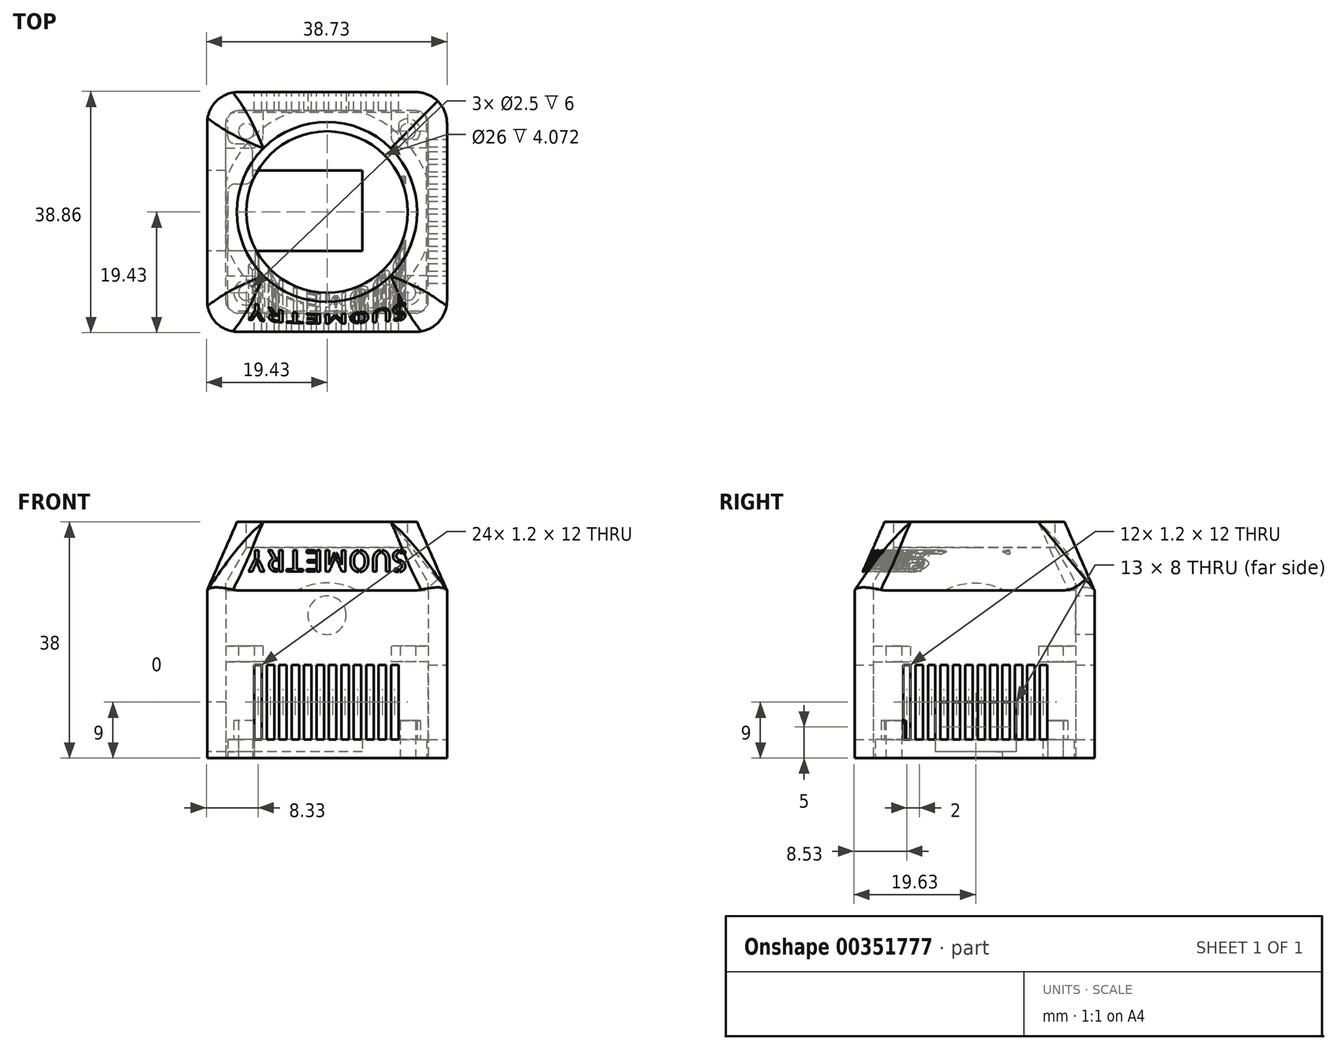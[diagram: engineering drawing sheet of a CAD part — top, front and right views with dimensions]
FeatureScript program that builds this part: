
annotation { "Feature Type Name" : "Feature", "Feature Type Description" : "" }
export const myFeature = defineFeature(function(context is Context, id is Id, definition is map)
    precondition{}
    {
        {
            var Q0;
            Q0=qCreatedBy(makeId("Top.planeOp"),FACE);
            var sketch = newSketch(context, id + "F0", { "sketchPlane" : qUnion([Q0])});
            skLineSegment(sketch, "E0.bottom", {"start": v(16, -16) * mm, "end": v(-16, -16) * mm});
            skLineSegment(sketch, "E0.top", {"start": v(16, 16) * mm, "end": v(-16, 16) * mm});
            skLineSegment(sketch, "E0.left", {"start": v(16, -16) * mm, "end": v(16, 16) * mm});
            skLineSegment(sketch, "E0.right", {"start": v(-16, -16) * mm, "end": v(-16, 16) * mm});
            skPoint(sketch, "E0.middle", {"position": v(0, 0) * mm});
            skCircle(sketch, "E1", {"center": v(-13, 13) * mm, "radius": 1.25 * mm});
            skCircle(sketch, "E2", {"center": v(13, 13) * mm, "radius": 1.25 * mm});
            skCircle(sketch, "E3", {"center": v(13, -13) * mm, "radius": 1.25 * mm});
            skCircle(sketch, "E4", {"center": v(-13, -13) * mm, "radius": 1.25 * mm});
            skLineSegment(sketch, "E5.bottom", {"start": v(-16, 4.5) * mm, "end": v(-12, 4.5) * mm});
            skLineSegment(sketch, "E5.top", {"start": v(-16, 11) * mm, "end": v(-12, 11) * mm});
            skLineSegment(sketch, "E5.left", {"start": v(-16, 4.5) * mm, "end": v(-16, 11) * mm});
            skLineSegment(sketch, "E5.right", {"start": v(-12, 4.5) * mm, "end": v(-12, 11) * mm});
            skSolve(sketch);
        }
        {
            var Q0;
            {var subQ4=sQuery(id+"F0.wireOp",EDGE,"E0.bottom");Q0=makeQuery(id+"F0.imprint","IMPRINT",FACE,{"disambiguationData":[TD([[makeQuery(id+"F0.imprint","IMPRINT",EDGE,{"derivedFrom":subQ4}),-1.0]])]});}
            var Q1;
            Q1=makeQuery(id+"F0.imprint","IMPRINT",FACE,{"disambiguationData":[TD([[makeQuery(id+"F0.imprint","IMPRINT",EDGE,{"derivedFrom":sQuery(id+"F0.wireOp",EDGE,"E4")}),1.0]])]});
            var Q2;
            Q2=makeQuery(id+"F0.imprint","IMPRINT",FACE,{"disambiguationData":[TD([[makeQuery(id+"F0.imprint","IMPRINT",EDGE,{"derivedFrom":sQuery(id+"F0.wireOp",EDGE,"E3")}),1.0]])]});
            var Q3;
            Q3=makeQuery(id+"F0.imprint","IMPRINT",FACE,{"disambiguationData":[TD([[makeQuery(id+"F0.imprint","IMPRINT",EDGE,{"derivedFrom":sQuery(id+"F0.wireOp",EDGE,"E2")}),1.0]])]});
            var Q4;
            Q4=makeQuery(id+"F0.imprint","IMPRINT",FACE,{"disambiguationData":[TD([[makeQuery(id+"F0.imprint","IMPRINT",EDGE,{"derivedFrom":sQuery(id+"F0.wireOp",EDGE,"E1")}),1.0]])]});
            extrude(context, id + "F1", {"entities" : qUnion([Q0, Q1, Q2, Q3, Q4]), "depth" : 3 * mm, "offsetDistance" : 25 * mm});
        }
        {
            var Q0;
            Q0=qCreatedBy(makeId("Top.planeOp"),FACE);
            var sketch = newSketch(context, id + "F2", { "sketchPlane" : qUnion([Q0])});
            skLineSegment(sketch, "E6.bottom", {"start": v(16.3, -16.3) * mm, "end": v(-16.3, -16.3) * mm});
            skLineSegment(sketch, "E6.top", {"start": v(16.3, 16.3) * mm, "end": v(-16.3, 16.3) * mm});
            skLineSegment(sketch, "E6.left", {"start": v(16.3, -16.3) * mm, "end": v(16.3, 16.3) * mm});
            skLineSegment(sketch, "E6.right", {"start": v(-16.3, -16.3) * mm, "end": v(-16.3, 16.3) * mm});
            skPoint(sketch, "E6.middle", {"position": v(0, 0) * mm});
            skLineSegment(sketch, "E7.0", {"start": v(19.3, 19.3) * mm, "end": v(-19.3, 19.3) * mm});
            skLineSegment(sketch, "E7.1", {"start": v(19.3, -19.3) * mm, "end": v(19.3, 19.3) * mm});
            skLineSegment(sketch, "E7.2", {"start": v(19.3, -19.3) * mm, "end": v(-19.3, -19.3) * mm});
            skLineSegment(sketch, "E7.3", {"start": v(-19.3, -19.3) * mm, "end": v(-19.3, 19.3) * mm});
            skLineSegment(sketch, "E8.bottom", {"start": v(-16.3, -16.3) * mm, "end": v(-10.3, -16.3) * mm});
            skLineSegment(sketch, "E8.top", {"start": v(-16.3, -10.3) * mm, "end": v(-10.3, -10.3) * mm});
            skLineSegment(sketch, "E8.left", {"start": v(-16.3, -16.3) * mm, "end": v(-16.3, -10.3) * mm});
            skLineSegment(sketch, "E8.right", {"start": v(-10.3, -16.3) * mm, "end": v(-10.3, -10.3) * mm});
            skLineSegment(sketch, "E9.bottom", {"start": v(-16.3, 16.3) * mm, "end": v(-10.3, 16.3) * mm});
            skLineSegment(sketch, "E9.top", {"start": v(-16.3, 10.3) * mm, "end": v(-10.3, 10.3) * mm});
            skLineSegment(sketch, "E9.left", {"start": v(-16.3, 16.3) * mm, "end": v(-16.3, 10.3) * mm});
            skLineSegment(sketch, "E9.right", {"start": v(-10.3, 16.3) * mm, "end": v(-10.3, 10.3) * mm});
            skLineSegment(sketch, "E10.bottom", {"start": v(16.3, 16.3) * mm, "end": v(10.3, 16.3) * mm});
            skLineSegment(sketch, "E10.top", {"start": v(16.3, 10.3) * mm, "end": v(10.3, 10.3) * mm});
            skLineSegment(sketch, "E10.left", {"start": v(16.3, 16.3) * mm, "end": v(16.3, 10.3) * mm});
            skLineSegment(sketch, "E10.right", {"start": v(10.3, 16.3) * mm, "end": v(10.3, 10.3) * mm});
            skLineSegment(sketch, "E11.bottom", {"start": v(16.3, -16.3) * mm, "end": v(10.3, -16.3) * mm});
            skLineSegment(sketch, "E11.top", {"start": v(16.3, -10.3) * mm, "end": v(10.3, -10.3) * mm});
            skLineSegment(sketch, "E11.left", {"start": v(16.3, -16.3) * mm, "end": v(16.3, -10.3) * mm});
            skLineSegment(sketch, "E11.right", {"start": v(10.3, -16.3) * mm, "end": v(10.3, -10.3) * mm});
            skSolve(sketch);
        }
        {
            var Q0;
            Q0=makeQuery(id+"F2.imprint","IMPRINT",FACE,{"disambiguationData":[TD([[makeQuery(id+"F2.imprint","IMPRINT",EDGE,{"derivedFrom":sQuery(id+"F2.wireOp",EDGE,"E6.bottom")}),1.0]])]});
            var sketch = newSketch(context, id + "F3", { "sketchPlane" : qUnion([Q0])});
            skCircle(sketch, "E12", {"center": v(13, -13) * mm, "radius": 2 * mm});
            skCircle(sketch, "E13", {"center": v(-13, -13) * mm, "radius": 2 * mm});
            skCircle(sketch, "E14", {"center": v(13, 13) * mm, "radius": 2 * mm});
            skCircle(sketch, "E15", {"center": v(-13, 13) * mm, "radius": 1.27 * mm});
            skSolve(sketch);
        }
        {
            var Q0;
            Q0=makeQuery(id+"F3.imprint","IMPRINT",FACE,{"disambiguationData":[TD([[makeQuery(id+"F3.imprint","IMPRINT",EDGE,{"derivedFrom":sQuery(id+"F3.wireOp",EDGE,"E13")}),1.0]])]});
            var Q1;
            Q1=makeQuery(id+"F3.imprint","IMPRINT",FACE,{"disambiguationData":[TD([[makeQuery(id+"F3.imprint","IMPRINT",EDGE,{"derivedFrom":sQuery(id+"F3.wireOp",EDGE,"E12")}),1.0]])]});
            var Q2;
            Q2=makeQuery(id+"F3.imprint","IMPRINT",FACE,{"disambiguationData":[TD([[makeQuery(id+"F3.imprint","IMPRINT",EDGE,{"derivedFrom":sQuery(id+"F3.wireOp",EDGE,"E14")}),1.0]])]});
            extrude(context, id + "F4", {"entities" : qUnion([Q0, Q1, Q2]), "operationType" : NewBodyOperationType.ADD, "depth" : 6 * mm, "offsetDistance" : 25 * mm});
        }
        {
            var Q0;
            Q0 = qSketchRegion(id + "F2", true);
            extrude(context, id + "F5", {"entities" : qUnion([Q0]), "depth" : 27 * mm, "offsetDistance" : 25 * mm});
        }
        {
            var Q0;
            Q0=makeQuery(id+"F5.opExtrude","SWEPT_FACE",FACE,{"disambiguationData":[OSD([sQuery(id+"F2.wireOp",EDGE,"E7.3")])]});
            var sketch = newSketch(context, id + "F6", { "sketchPlane" : qUnion([Q0])});
            skLineSegment(sketch, "E16.bottom", {"start": v(-6.7, 9) * mm, "end": v(6.3, 9) * mm});
            skLineSegment(sketch, "E16.top", {"start": v(-6.7, 1) * mm, "end": v(6.3, 1) * mm});
            skLineSegment(sketch, "E16.left", {"start": v(-6.7, 9) * mm, "end": v(-6.7, 1) * mm});
            skLineSegment(sketch, "E16.right", {"start": v(6.3, 9) * mm, "end": v(6.3, 1) * mm});
            skSolve(sketch);
        }
        {
            var Q0;
            Q0=makeQuery(id+"F6.imprint","IMPRINT",FACE,{"disambiguationData":[TD([[makeQuery(id+"F6.imprint","IMPRINT",EDGE,{"derivedFrom":sQuery(id+"F6.wireOp",EDGE,"E16.bottom")}),-1.0]])]});
            extrude(context, id + "F7", {"entities" : qUnion([Q0]), "operationType" : NewBodyOperationType.REMOVE, "oppositeDirection" : true, "depth" : 25 * mm, "offsetDistance" : 25 * mm});
        }
        {
            var Q0;
            Q0=qCreatedBy(makeId("Top.planeOp"),FACE);
            cPlane(context, id + "F8", {"entities" : qUnion([Q0]), "cplaneType" : CPlaneType.OFFSET, "offset" : 38 * mm, "width" : 150 * mm, "height" : 150 * mm});
        }
        {
            var Q0;
            Q0=qCreatedBy(id+"F8.planeOp",FACE);
            var sketch = newSketch(context, id + "F9", { "sketchPlane" : qUnion([Q0])});
            skCircle(sketch, "E17.0", {"center": v(0, 0) * mm, "radius": 14.5 * mm});
            skLineSegment(sketch, "E18", {"start": v(10.25, 10.25) * mm, "end": v(-10.25, -10.25) * mm, "construction": true});
            skPoint(sketch, "E19", {"position": v(10.25, 10.25) * mm});
            skLineSegment(sketch, "E20", {"start": v(-10.25, 10.25) * mm, "end": v(10.25, -10.25) * mm, "construction": true});
            skPoint(sketch, "E21", {"position": v(-10.25, 10.25) * mm});
            skPoint(sketch, "E22", {"position": v(-10.25, -10.25) * mm});
            skPoint(sketch, "E23", {"position": v(10.25, -10.25) * mm});
            skSolve(sketch);
        }
        {
            var Q0;
            Q0=qCreatedBy(makeId("Top.planeOp"),FACE);
            cPlane(context, id + "F10", {"entities" : qUnion([Q0]), "cplaneType" : CPlaneType.OFFSET, "offset" : 27 * mm, "width" : 150 * mm, "height" : 150 * mm});
        }
        {
            var Q0;
            Q0=qCreatedBy(id+"F10.planeOp",FACE);
            var sketch = newSketch(context, id + "F11", { "sketchPlane" : qUnion([Q0])});
            skLineSegment(sketch, "E24.bottom", {"start": v(19.3, -19.3) * mm, "end": v(-19.3, -19.3) * mm});
            skLineSegment(sketch, "E24.top", {"start": v(19.3, 19.3) * mm, "end": v(-19.3, 19.3) * mm});
            skLineSegment(sketch, "E24.left", {"start": v(19.3, -19.3) * mm, "end": v(19.3, 19.3) * mm});
            skLineSegment(sketch, "E24.right", {"start": v(-19.3, -19.3) * mm, "end": v(-19.3, 19.3) * mm});
            skPoint(sketch, "E24.middle", {"position": v(0, 0) * mm});
            skSolve(sketch);
        }
        {
            var Q0;
            Q0 = qSketchRegion(id + "F11", true);
            var Q1;
            Q1 = qSketchRegion(id + "F9", true);
            loft(context, id + "F12", {"operationType" : NewBodyOperationType.ADD, "sheetProfilesArray" : [{ "sheetProfileEntities" : qUnion([Q0]) }, { "sheetProfileEntities" : qUnion([Q1]) }]});
        }
        {
            var Q0;
            Q0=makeQuery(id+"F9.imprint","IMPRINT",FACE,{"disambiguationData":[TD([[makeQuery(id+"F9.imprint","IMPRINT",EDGE,{"derivedFrom":sQuery(id+"F9.wireOp",EDGE,"E17.0")}),1.0]])]});
            var sketch = newSketch(context, id + "F13", { "sketchPlane" : qUnion([Q0])});
            skCircle(sketch, "E25", {"center": v(0, 0) * mm, "radius": 13 * mm});
            skSolve(sketch);
        }
        {
            var Q0;
            Q0=makeQuery(id+"F13.imprint","IMPRINT",FACE,{"disambiguationData":[TD([[makeQuery(id+"F13.imprint","IMPRINT",EDGE,{"derivedFrom":sQuery(id+"F13.wireOp",EDGE,"E25")}),1.0]])]});
            extrude(context, id + "F14", {"entities" : qUnion([Q0]), "operationType" : NewBodyOperationType.REMOVE, "oppositeDirection" : true, "depth" : 25 * mm, "offsetDistance" : 25 * mm});
        }
        {
            var Q0;
            Q0=makeQuery(id+"F14.boolean.opBoolean","INTERSECT",EDGE,{"derivedFrom":[makeQuery(id+"F12.opLoft","CAP_FACE",FACE,{"disambiguationData":[OSD([makeQuery(id+"F11.imprint","IMPRINT",FACE,{"disambiguationData":[TD([[makeQuery(id+"F11.imprint","IMPRINT",EDGE,{"derivedFrom":sQuery(id+"F11.wireOp",EDGE,"E24.bottom")}),-1.0]])]})])],"isStart":true}),makeQuery(id+"F14.opExtrude","SWEPT_FACE",FACE,{"disambiguationData":[OSD([sQuery(id+"F13.wireOp",EDGE,"E25")])]})]});
            chamfer(context, id + "F15", {"entities" : qUnion([Q0]), "chamferType" : ChamferType.OFFSET_ANGLE, "width" : 4 * mm, "oppositeDirection" : false, "angle" : 60 * degree, "tangentPropagation" : true});
        }
        {
            var Q0;
            Q0=makeQuery(id+"F5.opExtrude","SWEPT_EDGE",EDGE,{"disambiguationData":[OSD([sQuery(id+"F2.wireOp",EDGE,"E7.1"),sQuery(id+"F2.wireOp",EDGE,"E7.2")])]});
            var Q1;
            Q1=makeQuery(id+"F12.opLoft","SWEPT_EDGE",EDGE,{"disambiguationData":[OSD([sQuery(id+"F11.wireOp",EDGE,"E24.bottom"),sQuery(id+"F11.wireOp",EDGE,"E24.left")])]});
            var Q2;
            Q2=makeQuery(id+"F12.opLoft","SWEPT_EDGE",EDGE,{"disambiguationData":[OSD([sQuery(id+"F9.wireOp",EDGE,"E17.0"),sQuery(id+"F11.wireOp",EDGE,"E24.bottom"),sQuery(id+"F11.wireOp",EDGE,"E24.top"),sQuery(id+"F11.wireOp",EDGE,"E24.left")])]});
            var Q3;
            Q3=makeQuery(id+"F5.opExtrude","SWEPT_EDGE",EDGE,{"disambiguationData":[OSD([sQuery(id+"F2.wireOp",EDGE,"E7.0"),sQuery(id+"F2.wireOp",EDGE,"E7.1")])]});
            var Q4;
            Q4=makeQuery(id+"F12.opLoft","SWEPT_EDGE",EDGE,{"disambiguationData":[OSD([sQuery(id+"F9.wireOp",EDGE,"E17.0"),sQuery(id+"F11.wireOp",EDGE,"E24.bottom"),sQuery(id+"F11.wireOp",EDGE,"E24.top"),sQuery(id+"F11.wireOp",EDGE,"E24.right")])]});
            var Q5;
            Q5=makeQuery(id+"F5.opExtrude","SWEPT_EDGE",EDGE,{"disambiguationData":[OSD([sQuery(id+"F2.wireOp",EDGE,"E7.2"),sQuery(id+"F2.wireOp",EDGE,"E7.3")])]});
            var Q6;
            Q6=makeQuery(id+"F5.opExtrude","SWEPT_EDGE",EDGE,{"disambiguationData":[OSD([sQuery(id+"F2.wireOp",EDGE,"E7.0"),sQuery(id+"F2.wireOp",EDGE,"E7.3")])]});
            var Q7;
            Q7=makeQuery(id+"F12.opLoft","SWEPT_EDGE",EDGE,{"disambiguationData":[OSD([sQuery(id+"F9.wireOp",EDGE,"E17.0"),sQuery(id+"F11.wireOp",EDGE,"E24.top"),sQuery(id+"F11.wireOp",EDGE,"E24.left"),sQuery(id+"F11.wireOp",EDGE,"E24.right")])]});
            fillet(context, id + "F16", {"entities" : qUnion([Q0, Q1, Q2, Q3, Q4, Q5, Q6, Q7]), "tangentPropagation" : true, "radius" : 5 * mm, "defaultsChanged" : true, "vertexSettings" : [], "allowEdgeOverflow" : false});
        }
        {
            var Q0;
            Q0=makeQuery(id+"F5.opExtrude","SWEPT_EDGE",EDGE,{"disambiguationData":[OSD([sQuery(id+"F2.wireOp",EDGE,"E6.bottom"),sQuery(id+"F2.wireOp",EDGE,"E6.right")])]});
            var Q1;
            Q1=makeQuery(id+"F5.opExtrude","SWEPT_EDGE",EDGE,{"disambiguationData":[OSD([sQuery(id+"F2.wireOp",EDGE,"E6.top"),sQuery(id+"F2.wireOp",EDGE,"E6.right")])]});
            var Q2;
            Q2=makeQuery(id+"F5.opExtrude","SWEPT_EDGE",EDGE,{"disambiguationData":[OSD([sQuery(id+"F2.wireOp",EDGE,"E6.top"),sQuery(id+"F2.wireOp",EDGE,"E6.left")])]});
            var Q3;
            Q3=makeQuery(id+"F5.opExtrude","SWEPT_EDGE",EDGE,{"disambiguationData":[OSD([sQuery(id+"F2.wireOp",EDGE,"E6.bottom"),sQuery(id+"F2.wireOp",EDGE,"E6.left")])]});
            fillet(context, id + "F17", {"entities" : qUnion([Q0, Q1, Q2, Q3]), "tangentPropagation" : true, "radius" : 2 * mm, "defaultsChanged" : true, "vertexSettings" : [], "allowEdgeOverflow" : false});
        }
        {
            var Q0;
            Q0=makeQuery(id+"F1.opExtrude","SWEPT_EDGE",EDGE,{"disambiguationData":[OSD([sQuery(id+"F0.wireOp",EDGE,"E0.bottom"),sQuery(id+"F0.wireOp",EDGE,"E0.right")])]});
            var Q1;
            Q1=makeQuery(id+"F1.opExtrude","SWEPT_EDGE",EDGE,{"disambiguationData":[OSD([sQuery(id+"F0.wireOp",EDGE,"E0.bottom"),sQuery(id+"F0.wireOp",EDGE,"E0.left")])]});
            var Q2;
            Q2=makeQuery(id+"F1.opExtrude","SWEPT_EDGE",EDGE,{"disambiguationData":[OSD([sQuery(id+"F0.wireOp",EDGE,"E0.top"),sQuery(id+"F0.wireOp",EDGE,"E0.left")])]});
            var Q3;
            Q3=makeQuery(id+"F1.opExtrude","SWEPT_EDGE",EDGE,{"disambiguationData":[OSD([sQuery(id+"F0.wireOp",EDGE,"E0.top"),sQuery(id+"F0.wireOp",EDGE,"E0.right")])]});
            var Q4;
            Q4=makeQuery(id+"F1.opExtrude","SWEPT_EDGE",EDGE,{"disambiguationData":[OSD([sQuery(id+"F0.wireOp",EDGE,"E5.top"),sQuery(id+"F0.wireOp",EDGE,"E5.right")])]});
            var Q5;
            Q5=makeQuery(id+"F1.opExtrude","SWEPT_EDGE",EDGE,{"disambiguationData":[OSD([sQuery(id+"F0.wireOp",EDGE,"E5.bottom"),sQuery(id+"F0.wireOp",EDGE,"E5.right")])]});
            var Q6;
            Q6=makeQuery(id+"F1.opExtrude","SWEPT_EDGE",EDGE,{"disambiguationData":[OSD([sQuery(id+"F0.wireOp",EDGE,"E0.right"),sQuery(id+"F0.wireOp",EDGE,"E5.top")])]});
            var Q7;
            Q7=makeQuery(id+"F1.opExtrude","SWEPT_EDGE",EDGE,{"disambiguationData":[OSD([sQuery(id+"F0.wireOp",EDGE,"E0.right"),sQuery(id+"F0.wireOp",EDGE,"E5.bottom")])]});
            fillet(context, id + "F18", {"entities" : qUnion([Q0, Q1, Q2, Q3, Q4, Q5, Q6, Q7]), "tangentPropagation" : true, "radius" : 1.2 * mm, "defaultsChanged" : true, "vertexSettings" : [], "allowEdgeOverflow" : false});
        }
        {
            var Q0;
            Q0=makeQuery(id+"F5.opExtrude","SWEPT_FACE",FACE,{"disambiguationData":[OSD([sQuery(id+"F2.wireOp",EDGE,"E7.2")])]});
            var sketch = newSketch(context, id + "F19", { "sketchPlane" : qUnion([Q0])});
            skCircle(sketch, "E26", {"center": v(0, 23) * mm, "radius": 3.1 * mm});
            skCircle(sketch, "E27", {"center": v(0, 23) * mm, "radius": 4.5 * mm});
            skSolve(sketch);
        }
        {
            var Q0;
            Q0=makeQuery(id+"F19.imprint","IMPRINT",FACE,{"disambiguationData":[TD([[makeQuery(id+"F19.imprint","IMPRINT",EDGE,{"derivedFrom":sQuery(id+"F19.wireOp",EDGE,"E26")}),1.0]])]});
            extrude(context, id + "F20", {"entities" : qUnion([Q0]), "operationType" : NewBodyOperationType.REMOVE, "oppositeDirection" : true, "depth" : 46.5 * mm, "offsetDistance" : 25 * mm, "hasSecondDirection" : true, "secondDirectionOppositeDirection" : true, "secondDirectionDepth" : 17.8 * mm});
        }
        {
            var Q0;
            {var subQ0=sQuery(id+"F2.wireOp",EDGE,"E7.2");Q0=makeQuery(id+"F19.imprint","IMPRINT",FACE,{"disambiguationData":[TD([[makeQuery(id+"F19.imprint","IMPRINT",EDGE,{"derivedFrom":makeQuery(id+"F5.opExtrude","CAP_EDGE",EDGE,{"disambiguationData":[OSD([subQ0])],"isStart":true})}),-1.0]])]});}
            var sketch = newSketch(context, id + "F21", { "sketchPlane" : qUnion([Q0])});
            skText(sketch, "E28", { "text": "SUOMETRY", "fontName": "AllertaStencil-Regular.ttf"});
            const initialGuessF21  = {"E28": [0.013, 0.03346, -1, 0, 0.00346]};
            skSetInitialGuess(sketch, initialGuessF21);
            skSolve(sketch);
        }
        {
            var Q0;
            Q0 = qSketchRegion(id + "F21", true);
            extrude(context, id + "F22", {"entities" : qUnion([Q0]), "operationType" : NewBodyOperationType.REMOVE, "oppositeDirection" : true, "depth" : 25 * mm, "offsetDistance" : 25 * mm});
        }
        {
            var Q0;
            Q0=makeQuery(id+"F5.opExtrude","SWEPT_FACE",FACE,{"disambiguationData":[OSD([sQuery(id+"F2.wireOp",EDGE,"E7.1")])]});
            var sketch = newSketch(context, id + "F23", { "sketchPlane" : qUnion([Q0])});
            skLineSegment(sketch, "E29.bottom", {"start": v(-10.3, 15) * mm, "end": v(-11.5, 15) * mm});
            skLineSegment(sketch, "E29.top", {"start": v(-11.5, 3) * mm, "end": v(-10.3, 3) * mm});
            skLineSegment(sketch, "E29.left", {"start": v(-11.5, 15) * mm, "end": v(-11.5, 3) * mm});
            skLineSegment(sketch, "E29.right", {"start": v(-10.3, 15) * mm, "end": v(-10.3, 3) * mm});
            skLineSegment(sketch, "E30.1.0.0", {"start": v(-8.3, 15) * mm, "end": v(-8.3, 3) * mm});
            skLineSegment(sketch, "E30.1.0.1", {"start": v(-9.5, 15) * mm, "end": v(-9.5, 3) * mm});
            skLineSegment(sketch, "E30.1.0.2", {"start": v(-8.3, 15) * mm, "end": v(-9.5, 15) * mm});
            skLineSegment(sketch, "E30.1.0.3", {"start": v(-9.5, 3) * mm, "end": v(-8.3, 3) * mm});
            skLineSegment(sketch, "E30.2.0.0", {"start": v(-6.3, 15) * mm, "end": v(-6.3, 3) * mm});
            skLineSegment(sketch, "E30.2.0.1", {"start": v(-7.5, 15) * mm, "end": v(-7.5, 3) * mm});
            skLineSegment(sketch, "E30.2.0.2", {"start": v(-6.3, 15) * mm, "end": v(-7.5, 15) * mm});
            skLineSegment(sketch, "E30.2.0.3", {"start": v(-7.5, 3) * mm, "end": v(-6.3, 3) * mm});
            skLineSegment(sketch, "E30.direction1", {"start": v(-11.5, 3) * mm, "end": v(-9.5, 3) * mm, "construction": true});
            skLineSegment(sketch, "E31.0.3.0", {"start": v(-4.3, 15) * mm, "end": v(-4.3, 3) * mm});
            skLineSegment(sketch, "E31.3.3.0", {"start": v(-5.5, 15) * mm, "end": v(-5.5, 3) * mm});
            skLineSegment(sketch, "E31.6.3.0", {"start": v(-4.3, 15) * mm, "end": v(-5.5, 15) * mm});
            skLineSegment(sketch, "E31.9.3.0", {"start": v(-5.5, 3) * mm, "end": v(-4.3, 3) * mm});
            skLineSegment(sketch, "E31.0.4.0", {"start": v(-2.3, 15) * mm, "end": v(-2.3, 3) * mm});
            skLineSegment(sketch, "E31.3.4.0", {"start": v(-3.5, 15) * mm, "end": v(-3.5, 3) * mm});
            skLineSegment(sketch, "E31.6.4.0", {"start": v(-2.3, 15) * mm, "end": v(-3.5, 15) * mm});
            skLineSegment(sketch, "E31.9.4.0", {"start": v(-3.5, 3) * mm, "end": v(-2.3, 3) * mm});
            skLineSegment(sketch, "E31.0.5.0", {"start": v(-0.3, 15) * mm, "end": v(-0.3, 3) * mm});
            skLineSegment(sketch, "E31.3.5.0", {"start": v(-1.5, 15) * mm, "end": v(-1.5, 3) * mm});
            skLineSegment(sketch, "E31.6.5.0", {"start": v(-0.3, 15) * mm, "end": v(-1.5, 15) * mm});
            skLineSegment(sketch, "E31.9.5.0", {"start": v(-1.5, 3) * mm, "end": v(-0.3, 3) * mm});
            skLineSegment(sketch, "E31.0.6.0", {"start": v(1.7, 15) * mm, "end": v(1.7, 3) * mm});
            skLineSegment(sketch, "E31.3.6.0", {"start": v(0.5, 15) * mm, "end": v(0.5, 3) * mm});
            skLineSegment(sketch, "E31.6.6.0", {"start": v(1.7, 15) * mm, "end": v(0.5, 15) * mm});
            skLineSegment(sketch, "E31.9.6.0", {"start": v(0.5, 3) * mm, "end": v(1.7, 3) * mm});
            skLineSegment(sketch, "E31.0.7.0", {"start": v(3.7, 15) * mm, "end": v(3.7, 3) * mm});
            skLineSegment(sketch, "E31.3.7.0", {"start": v(2.5, 15) * mm, "end": v(2.5, 3) * mm});
            skLineSegment(sketch, "E31.6.7.0", {"start": v(3.7, 15) * mm, "end": v(2.5, 15) * mm});
            skLineSegment(sketch, "E31.9.7.0", {"start": v(2.5, 3) * mm, "end": v(3.7, 3) * mm});
            skLineSegment(sketch, "E31.0.8.0", {"start": v(5.7, 15) * mm, "end": v(5.7, 3) * mm});
            skLineSegment(sketch, "E31.3.8.0", {"start": v(4.5, 15) * mm, "end": v(4.5, 3) * mm});
            skLineSegment(sketch, "E31.6.8.0", {"start": v(5.7, 15) * mm, "end": v(4.5, 15) * mm});
            skLineSegment(sketch, "E31.9.8.0", {"start": v(4.5, 3) * mm, "end": v(5.7, 3) * mm});
            skLineSegment(sketch, "E31.0.9.0", {"start": v(7.7, 15) * mm, "end": v(7.7, 3) * mm});
            skLineSegment(sketch, "E31.3.9.0", {"start": v(6.5, 15) * mm, "end": v(6.5, 3) * mm});
            skLineSegment(sketch, "E31.6.9.0", {"start": v(7.7, 15) * mm, "end": v(6.5, 15) * mm});
            skLineSegment(sketch, "E31.9.9.0", {"start": v(6.5, 3) * mm, "end": v(7.7, 3) * mm});
            skLineSegment(sketch, "E31.0.10.0", {"start": v(9.7, 15) * mm, "end": v(9.7, 3) * mm});
            skLineSegment(sketch, "E31.3.10.0", {"start": v(8.5, 15) * mm, "end": v(8.5, 3) * mm});
            skLineSegment(sketch, "E31.6.10.0", {"start": v(9.7, 15) * mm, "end": v(8.5, 15) * mm});
            skLineSegment(sketch, "E31.9.10.0", {"start": v(8.5, 3) * mm, "end": v(9.7, 3) * mm});
            skLineSegment(sketch, "E31.0.11.0", {"start": v(11.7, 15) * mm, "end": v(11.7, 3) * mm});
            skLineSegment(sketch, "E31.3.11.0", {"start": v(10.5, 15) * mm, "end": v(10.5, 3) * mm});
            skLineSegment(sketch, "E31.6.11.0", {"start": v(11.7, 15) * mm, "end": v(10.5, 15) * mm});
            skLineSegment(sketch, "E31.9.11.0", {"start": v(10.5, 3) * mm, "end": v(11.7, 3) * mm});
            skSolve(sketch);
        }
        {
            var Q0;
            Q0=makeQuery(id+"F23.imprint","IMPRINT",FACE,{"disambiguationData":[TD([[makeQuery(id+"F23.imprint","IMPRINT",EDGE,{"derivedFrom":sQuery(id+"F23.wireOp",EDGE,"E31.0.11.0")}),-1.0]])]});
            var Q1;
            Q1=makeQuery(id+"F23.imprint","IMPRINT",FACE,{"disambiguationData":[TD([[makeQuery(id+"F23.imprint","IMPRINT",EDGE,{"derivedFrom":sQuery(id+"F23.wireOp",EDGE,"E31.0.10.0")}),-1.0]])]});
            var Q2;
            Q2 = qSketchRegion(id + "F23", true);
            extrude(context, id + "F24", {"entities" : qUnion([Q0, Q1, Q2]), "operationType" : NewBodyOperationType.REMOVE, "oppositeDirection" : true, "depth" : 30.6 * mm, "offsetDistance" : 25 * mm});
        }
        {
            var Q0;
            Q0=makeQuery(id+"F5.opExtrude","SWEPT_FACE",FACE,{"disambiguationData":[OSD([sQuery(id+"F2.wireOp",EDGE,"E7.0")])]});
            var sketch = newSketch(context, id + "F25", { "sketchPlane" : qUnion([Q0])});
            skLineSegment(sketch, "E32.bottom", {"start": v(-11.5, 3) * mm, "end": v(-10.3, 3) * mm});
            skLineSegment(sketch, "E32.top", {"start": v(-11.5, 15) * mm, "end": v(-10.3, 15) * mm});
            skLineSegment(sketch, "E32.left", {"start": v(-11.5, 3) * mm, "end": v(-11.5, 15) * mm});
            skLineSegment(sketch, "E32.right", {"start": v(-10.3, 3) * mm, "end": v(-10.3, 15) * mm});
            skLineSegment(sketch, "E33.1.0.0", {"start": v(-8.3, 3) * mm, "end": v(-8.3, 15) * mm});
            skLineSegment(sketch, "E33.1.0.1", {"start": v(-9.5, 15) * mm, "end": v(-8.3, 15) * mm});
            skLineSegment(sketch, "E33.1.0.2", {"start": v(-9.5, 3) * mm, "end": v(-9.5, 15) * mm});
            skLineSegment(sketch, "E33.1.0.3", {"start": v(-9.5, 3) * mm, "end": v(-8.3, 3) * mm});
            skLineSegment(sketch, "E33.2.0.0", {"start": v(-6.3, 3) * mm, "end": v(-6.3, 15) * mm});
            skLineSegment(sketch, "E33.2.0.1", {"start": v(-7.5, 15) * mm, "end": v(-6.3, 15) * mm});
            skLineSegment(sketch, "E33.2.0.2", {"start": v(-7.5, 3) * mm, "end": v(-7.5, 15) * mm});
            skLineSegment(sketch, "E33.2.0.3", {"start": v(-7.5, 3) * mm, "end": v(-6.3, 3) * mm});
            skLineSegment(sketch, "E33.3.0.0", {"start": v(-4.3, 3) * mm, "end": v(-4.3, 15) * mm});
            skLineSegment(sketch, "E33.3.0.1", {"start": v(-5.5, 15) * mm, "end": v(-4.3, 15) * mm});
            skLineSegment(sketch, "E33.3.0.2", {"start": v(-5.5, 3) * mm, "end": v(-5.5, 15) * mm});
            skLineSegment(sketch, "E33.3.0.3", {"start": v(-5.5, 3) * mm, "end": v(-4.3, 3) * mm});
            skLineSegment(sketch, "E33.4.0.0", {"start": v(-2.3, 3) * mm, "end": v(-2.3, 15) * mm});
            skLineSegment(sketch, "E33.4.0.1", {"start": v(-3.5, 15) * mm, "end": v(-2.3, 15) * mm});
            skLineSegment(sketch, "E33.4.0.2", {"start": v(-3.5, 3) * mm, "end": v(-3.5, 15) * mm});
            skLineSegment(sketch, "E33.4.0.3", {"start": v(-3.5, 3) * mm, "end": v(-2.3, 3) * mm});
            skLineSegment(sketch, "E33.5.0.0", {"start": v(-0.3, 3) * mm, "end": v(-0.3, 15) * mm});
            skLineSegment(sketch, "E33.5.0.1", {"start": v(-1.5, 15) * mm, "end": v(-0.3, 15) * mm});
            skLineSegment(sketch, "E33.5.0.2", {"start": v(-1.5, 3) * mm, "end": v(-1.5, 15) * mm});
            skLineSegment(sketch, "E33.5.0.3", {"start": v(-1.5, 3) * mm, "end": v(-0.3, 3) * mm});
            skLineSegment(sketch, "E33.6.0.0", {"start": v(1.7, 3) * mm, "end": v(1.7, 15) * mm});
            skLineSegment(sketch, "E33.6.0.1", {"start": v(0.5, 15) * mm, "end": v(1.7, 15) * mm});
            skLineSegment(sketch, "E33.6.0.2", {"start": v(0.5, 3) * mm, "end": v(0.5, 15) * mm});
            skLineSegment(sketch, "E33.6.0.3", {"start": v(0.5, 3) * mm, "end": v(1.7, 3) * mm});
            skLineSegment(sketch, "E33.7.0.0", {"start": v(3.7, 3) * mm, "end": v(3.7, 15) * mm});
            skLineSegment(sketch, "E33.7.0.1", {"start": v(2.5, 15) * mm, "end": v(3.7, 15) * mm});
            skLineSegment(sketch, "E33.7.0.2", {"start": v(2.5, 3) * mm, "end": v(2.5, 15) * mm});
            skLineSegment(sketch, "E33.7.0.3", {"start": v(2.5, 3) * mm, "end": v(3.7, 3) * mm});
            skLineSegment(sketch, "E33.8.0.0", {"start": v(5.7, 3) * mm, "end": v(5.7, 15) * mm});
            skLineSegment(sketch, "E33.8.0.1", {"start": v(4.5, 15) * mm, "end": v(5.7, 15) * mm});
            skLineSegment(sketch, "E33.8.0.2", {"start": v(4.5, 3) * mm, "end": v(4.5, 15) * mm});
            skLineSegment(sketch, "E33.8.0.3", {"start": v(4.5, 3) * mm, "end": v(5.7, 3) * mm});
            skLineSegment(sketch, "E33.9.0.0", {"start": v(7.7, 3) * mm, "end": v(7.7, 15) * mm});
            skLineSegment(sketch, "E33.9.0.1", {"start": v(6.5, 15) * mm, "end": v(7.7, 15) * mm});
            skLineSegment(sketch, "E33.9.0.2", {"start": v(6.5, 3) * mm, "end": v(6.5, 15) * mm});
            skLineSegment(sketch, "E33.9.0.3", {"start": v(6.5, 3) * mm, "end": v(7.7, 3) * mm});
            skLineSegment(sketch, "E33.10.0.0", {"start": v(9.7, 3) * mm, "end": v(9.7, 15) * mm});
            skLineSegment(sketch, "E33.10.0.1", {"start": v(8.5, 15) * mm, "end": v(9.7, 15) * mm});
            skLineSegment(sketch, "E33.10.0.2", {"start": v(8.5, 3) * mm, "end": v(8.5, 15) * mm});
            skLineSegment(sketch, "E33.10.0.3", {"start": v(8.5, 3) * mm, "end": v(9.7, 3) * mm});
            skLineSegment(sketch, "E33.direction1", {"start": v(-10.3, 3) * mm, "end": v(-8.3, 3) * mm, "construction": true});
            skLineSegment(sketch, "E34.0.11.0", {"start": v(11.7, 3) * mm, "end": v(11.7, 15) * mm});
            skLineSegment(sketch, "E34.3.11.0", {"start": v(10.5, 15) * mm, "end": v(11.7, 15) * mm});
            skLineSegment(sketch, "E34.6.11.0", {"start": v(10.5, 3) * mm, "end": v(10.5, 15) * mm});
            skLineSegment(sketch, "E34.9.11.0", {"start": v(10.5, 3) * mm, "end": v(11.7, 3) * mm});
            skSolve(sketch);
        }
        {
            var Q0;
            Q0 = qSketchRegion(id + "F25", true);
            extrude(context, id + "F26", {"entities" : qUnion([Q0]), "operationType" : NewBodyOperationType.REMOVE, "oppositeDirection" : true, "depth" : 48.4 * mm, "offsetDistance" : 25 * mm});
        }
        {
            var Q0;
            {var subQ4=sQuery(id+"F2.wireOp",EDGE,"E8.top");Q0=makeQuery(id+"F2.imprint","IMPRINT",FACE,{"disambiguationData":[TD([[makeQuery(id+"F2.imprint","IMPRINT",EDGE,{"derivedFrom":subQ4}),-1.0]])]});}
            var Q1;
            {var subQ4=sQuery(id+"F2.wireOp",EDGE,"E11.top");Q1=makeQuery(id+"F2.imprint","IMPRINT",FACE,{"disambiguationData":[TD([[makeQuery(id+"F2.imprint","IMPRINT",EDGE,{"derivedFrom":subQ4}),1.0]])]});}
            var Q2;
            {var subQ4=sQuery(id+"F2.wireOp",EDGE,"E10.top");Q2=makeQuery(id+"F2.imprint","IMPRINT",FACE,{"disambiguationData":[TD([[makeQuery(id+"F2.imprint","IMPRINT",EDGE,{"derivedFrom":subQ4}),-1.0]])]});}
            var Q3;
            {var subQ4=sQuery(id+"F2.wireOp",EDGE,"E9.top");Q3=makeQuery(id+"F2.imprint","IMPRINT",FACE,{"disambiguationData":[TD([[makeQuery(id+"F2.imprint","IMPRINT",EDGE,{"derivedFrom":subQ4}),1.0]])]});}
            extrude(context, id + "F27", {"entities" : qUnion([Q0, Q1, Q2, Q3]), "operationType" : NewBodyOperationType.ADD, "depth" : 18 * mm, "offsetDistance" : 25 * mm, "hasSecondDirection" : true, "secondDirectionOppositeDirection" : false, "secondDirectionDepth" : 15.5 * mm});
        }
        {
            var Q0;
            Q0=sQuery(id+"F3.wireOp",VERTEX,"E13.center");
            var Q1;
            Q1=sQuery(id+"F3.wireOp",VERTEX,"E12.center");
            var Q2;
            Q2=sQuery(id+"F3.wireOp",VERTEX,"E14.center");
            var Q3;
            Q3=sQuery(id+"F3.wireOp",VERTEX,"E15.center");
            var Q4;
            Q4=makeQuery(id+"F1.opExtrude","SWEPT_BODY",BODY,{"disambiguationData":[OSD([sQuery(id+"F0.wireOp",EDGE,"E0.bottom"),sQuery(id+"F0.wireOp",EDGE,"E0.top"),sQuery(id+"F0.wireOp",EDGE,"E0.left"),sQuery(id+"F0.wireOp",EDGE,"E0.right"),sQuery(id+"F0.wireOp",EDGE,"E5.bottom"),sQuery(id+"F0.wireOp",EDGE,"E5.top"),sQuery(id+"F0.wireOp",EDGE,"E5.right")])]});
            var Q5;
            Q5=makeQuery(id+"F5.opExtrude","SWEPT_BODY",BODY,{"disambiguationData":[OSD([sQuery(id+"F2.wireOp",EDGE,"E6.bottom"),sQuery(id+"F2.wireOp",EDGE,"E6.top"),sQuery(id+"F2.wireOp",EDGE,"E6.left"),sQuery(id+"F2.wireOp",EDGE,"E6.right"),sQuery(id+"F2.wireOp",EDGE,"E7.0"),sQuery(id+"F2.wireOp",EDGE,"E7.1"),sQuery(id+"F2.wireOp",EDGE,"E7.2"),sQuery(id+"F2.wireOp",EDGE,"E7.3")])]});
            hole(context, id + "F28", {"style" : HoleStyle.SIMPLE, "endStyle" : HoleEndStyle.BLIND, "oppositeDirection" : true, "holeDiameter" : 2.5 * mm, "majorDiameter" : 5 * mm, "holeDepth" : 25 * mm, "isTappedThrough" : true, "tappedDepth" : 12 * mm, "tapClearance" : 3, "locations" : qUnion([Q0, Q1, Q2, Q3]), "scope" : qUnion([Q4, Q5])});
        }
        {
            var Q0;
            Q0=makeQuery(id+"F27.opExtrude","SWEPT_EDGE",EDGE,{"disambiguationData":[OSD([sQuery(id+"F2.wireOp",EDGE,"E9.top"),sQuery(id+"F2.wireOp",EDGE,"E9.right")])]});
            var Q1;
            Q1=makeQuery(id+"F27.opExtrude","SWEPT_EDGE",EDGE,{"disambiguationData":[OSD([sQuery(id+"F2.wireOp",EDGE,"E8.top"),sQuery(id+"F2.wireOp",EDGE,"E8.right")])]});
            var Q2;
            Q2=makeQuery(id+"F27.opExtrude","SWEPT_EDGE",EDGE,{"disambiguationData":[OSD([sQuery(id+"F2.wireOp",EDGE,"E11.top"),sQuery(id+"F2.wireOp",EDGE,"E11.right")])]});
            var Q3;
            Q3=makeQuery(id+"F27.opExtrude","SWEPT_EDGE",EDGE,{"disambiguationData":[OSD([sQuery(id+"F2.wireOp",EDGE,"E10.top"),sQuery(id+"F2.wireOp",EDGE,"E10.right")])]});
            fillet(context, id + "F29", {"entities" : qUnion([Q0, Q1, Q2, Q3]), "tangentPropagation" : true, "radius" : 2 * mm, "defaultsChanged" : true, "vertexSettings" : [], "allowEdgeOverflow" : false});
        }
    });
